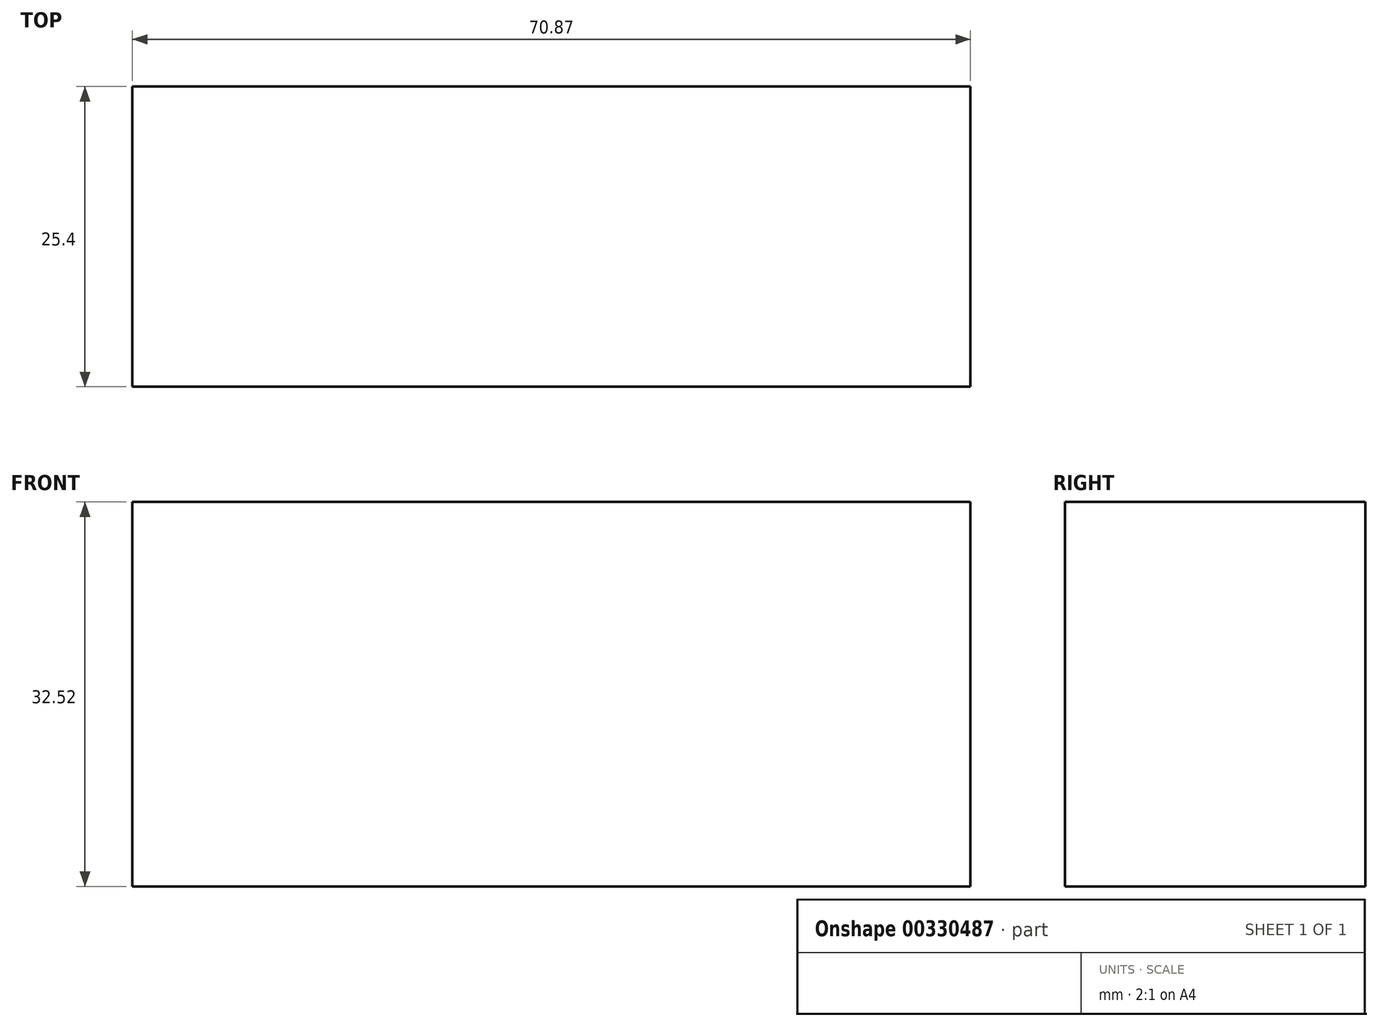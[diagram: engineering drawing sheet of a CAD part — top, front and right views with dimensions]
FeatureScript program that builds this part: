
annotation { "Feature Type Name" : "Feature", "Feature Type Description" : "" }
export const myFeature = defineFeature(function(context is Context, id is Id, definition is map)
    precondition{}
    {
        {
            var Q0;
            Q0=qCreatedBy(makeId("Front.planeOp"),FACE);
            var sketch = newSketch(context, id + "F0", { "sketchPlane" : qUnion([Q0])});
            skLineSegment(sketch, "E0.bottom", {"start": v(0, -25.01) * mm, "end": v(-70.87, -25.01) * mm});
            skLineSegment(sketch, "E0.top", {"start": v(0, -57.53) * mm, "end": v(-70.87, -57.53) * mm});
            skLineSegment(sketch, "E0.left", {"start": v(0, -25.01) * mm, "end": v(0, -57.53) * mm});
            skLineSegment(sketch, "E0.right", {"start": v(-70.87, -25.01) * mm, "end": v(-70.87, -57.53) * mm});
            skSolve(sketch);
        }
        {
            var Q0;
            Q0 = qSketchRegion(id + "F0", true);
            extrude(context, id + "F1", {"entities" : qUnion([Q0]), "depth" : 25.4 * mm});
        }
    });
